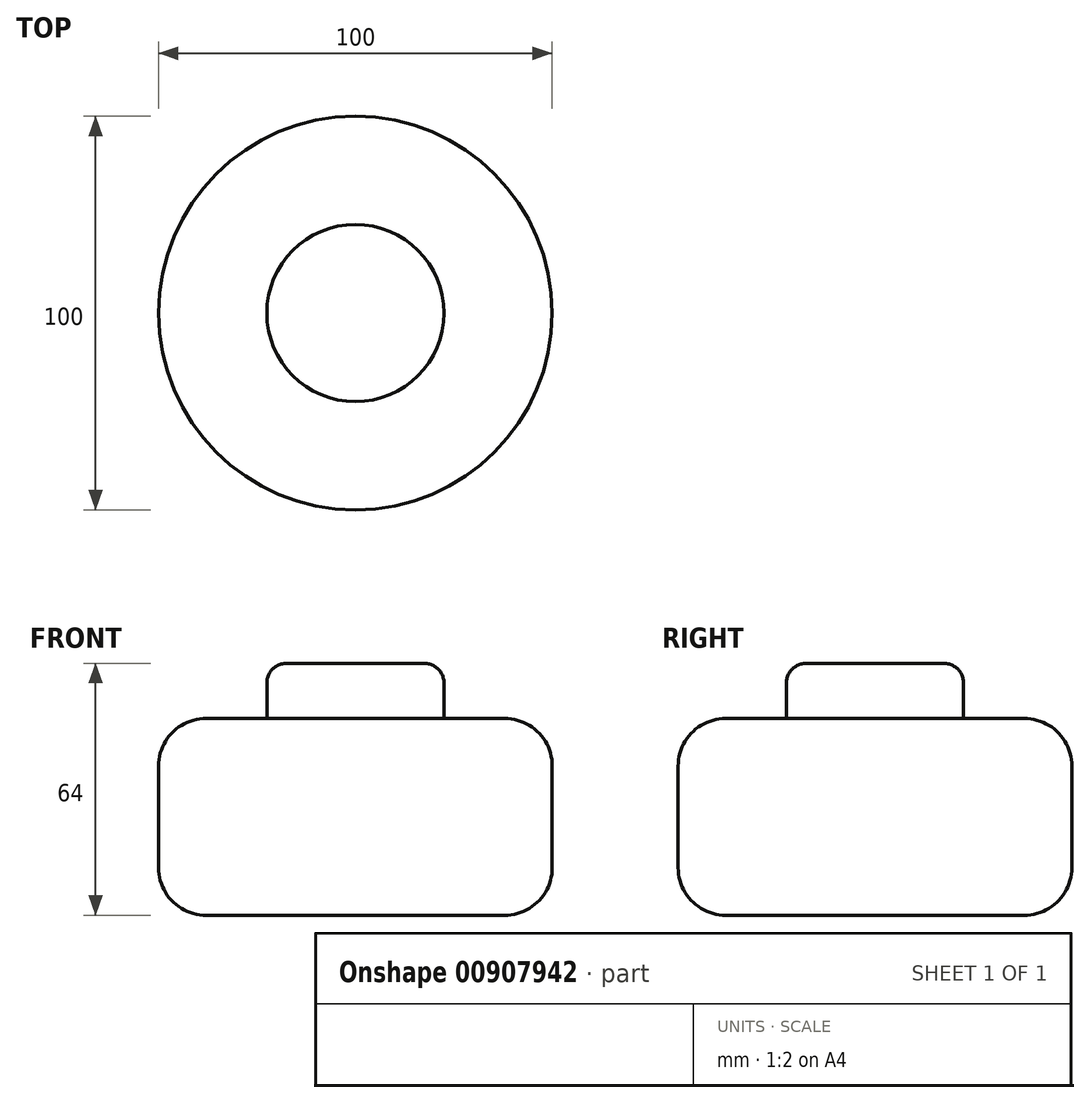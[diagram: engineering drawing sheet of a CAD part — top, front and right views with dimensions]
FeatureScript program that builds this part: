
annotation { "Feature Type Name" : "Feature", "Feature Type Description" : "" }
export const myFeature = defineFeature(function(context is Context, id is Id, definition is map)
    precondition{}
    {
        {
            var Q0;
            Q0=qCreatedBy(makeId("Top.planeOp"),FACE);
            var sketch = newSketch(context, id + "F0", { "sketchPlane" : qUnion([Q0])});
            skCircle(sketch, "E0", {"center": v(0, 0) * mm, "radius": 50 * mm});
            skSolve(sketch);
        }
        {
            var Q0;
            Q0=makeQuery(id+"F0.imprint","IMPRINT",FACE,{"disambiguationData":[TD([[makeQuery(id+"F0.imprint","IMPRINT",EDGE,{"derivedFrom":sQuery(id+"F0.wireOp",EDGE,"E0")}),1.0]])]});
            extrude(context, id + "F1", {"entities" : qUnion([Q0]), "depth" : 50 * mm, "offsetDistance" : 25 * mm});
        }
        {
            var Q0;
            Q0=makeQuery(id+"F1.opExtrude","CAP_EDGE",EDGE,{"disambiguationData":[OSD([sQuery(id+"F0.wireOp",EDGE,"E0")])],"isStart":false});
            var Q1;
            Q1=makeQuery(id+"F1.opExtrude","CAP_EDGE",EDGE,{"disambiguationData":[OSD([sQuery(id+"F0.wireOp",EDGE,"E0")])],"isStart":true});
            fillet(context, id + "F2", {"entities" : qUnion([Q0, Q1]), "radius" : 12.07 * mm, "tangentPropagation" : true, "allowEdgeOverflow" : false});
        }
        {
            var Q0;
            Q0=makeQuery(id+"F1.opExtrude","CAP_FACE",FACE,{"disambiguationData":[OSD([sQuery(id+"F0.wireOp",EDGE,"E0")])],"isStart":false});
            var sketch = newSketch(context, id + "F3", { "sketchPlane" : qUnion([Q0])});
            skCircle(sketch, "E1", {"center": v(0, 0) * mm, "radius": 22.5 * mm});
            skSolve(sketch);
        }
        {
            var Q0;
            Q0=makeQuery(id+"F3.imprint","IMPRINT",FACE,{"disambiguationData":[TD([[makeQuery(id+"F3.imprint","IMPRINT",EDGE,{"derivedFrom":sQuery(id+"F3.wireOp",EDGE,"E1")}),1.0]])]});
            extrude(context, id + "F4", {"entities" : qUnion([Q0]), "operationType" : NewBodyOperationType.ADD, "depth" : 14 * mm, "offsetDistance" : 25 * mm});
        }
        {
            var Q0;
            Q0=makeQuery(id+"F4.opExtrude","CAP_EDGE",EDGE,{"disambiguationData":[OSD([sQuery(id+"F3.wireOp",EDGE,"E1")])],"isStart":false});
            fillet(context, id + "F5", {"entities" : qUnion([Q0]), "radius" : 5 * mm, "tangentPropagation" : true, "allowEdgeOverflow" : false});
        }
    });
